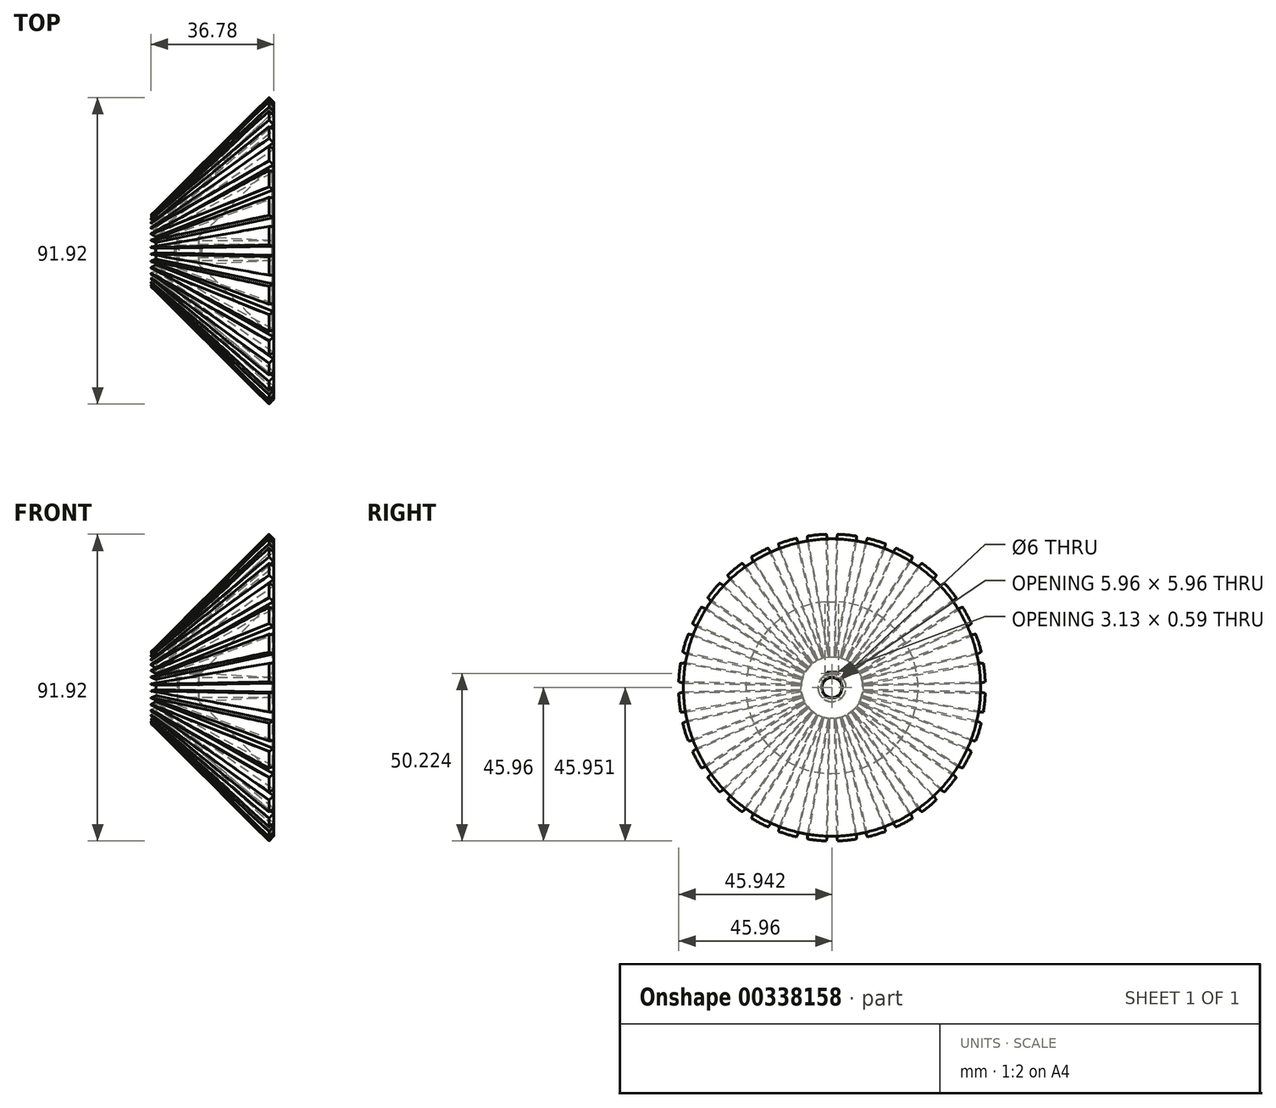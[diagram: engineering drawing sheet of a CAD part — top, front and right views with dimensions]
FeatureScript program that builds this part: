
annotation { "Feature Type Name" : "Feature", "Feature Type Description" : "" }
export const myFeature = defineFeature(function(context is Context, id is Id, definition is map)
    precondition{}
    {
        {
            var Q0;
            Q0=qCreatedBy(makeId("Front.planeOp"),FACE);
            var sketch = newSketch(context, id + "F0", { "sketchPlane" : qUnion([Q0])});
            skLineSegment(sketch, "E0", {"start": v(0, 0) * mm, "end": v(35.34, 35.34) * mm});
            skLineSegment(sketch, "E1", {"start": v(0, 0) * mm, "end": v(38.3, 0) * mm});
            skLineSegment(sketch, "E2", {"start": v(0, 0) * mm, "end": v(-10.6, 10.6) * mm});
            skLineSegment(sketch, "E3", {"start": v(-10.6, 10.6) * mm, "end": v(24.73, 45.94) * mm});
            skLineSegment(sketch, "E4", {"start": v(24.73, 45.94) * mm, "end": v(35.34, 35.34) * mm});
            skSolve(sketch);
        }
        {
            var Q0;
            Q0=makeQuery(id+"F0.imprint","IMPRINT",FACE,{"disambiguationData":[TD([[makeQuery(id+"F0.imprint","IMPRINT",EDGE,{"derivedFrom":sQuery(id+"F0.wireOp",EDGE,"E0")}),1.0]])]});
            extrude(context, id + "F1", {"entities" : qUnion([Q0]), "endBound" : BoundingType.SYMMETRIC, "depth" : 4 * mm});
        }
        {
            var Q0;
            Q0=makeQuery(id+"F1.opExtrude","SWEPT_FACE",FACE,{"disambiguationData":[OSD([sQuery(id+"F0.wireOp",EDGE,"E3")])]});
            var sketch = newSketch(context, id + "F2", { "sketchPlane" : qUnion([Q0])});
            skPoint(sketch, "E5", {"position": v(-2, 49.97) * mm});
            skPoint(sketch, "E6", {"position": v(-1, -0.02) * mm});
            skLineSegment(sketch, "E7", {"start": v(-1, -0.02) * mm, "end": v(1, 0.02) * mm, "construction": true});
            skPoint(sketch, "E8", {"position": v(0, 0) * mm});
            skLineSegment(sketch, "E9", {"start": v(0, -8) * mm, "end": v(0, -12.28) * mm, "construction": true});
            skLineSegment(sketch, "E10", {"start": v(1.74, 52.97) * mm, "end": v(-1.74, 52.97) * mm});
            skLineSegment(sketch, "E11", {"start": v(0.94, -3.02) * mm, "end": v(-0.94, -3.02) * mm});
            skLineSegment(sketch, "E12", {"start": v(-0.94, -3.02) * mm, "end": v(-1.74, 52.97) * mm});
            skLineSegment(sketch, "E13.MirrorCS", {"start": v(0.94, -3.02) * mm, "end": v(1.74, 52.97) * mm});
            skSolve(sketch);
        }
        {
            var Q0;
            Q0=qCreatedBy(makeId("Top.planeOp"),FACE);
            var sketch = newSketch(context, id + "F3", { "sketchPlane" : qUnion([Q0])});
            skLineSegment(sketch, "E14", {"start": v(0, 0) * mm, "end": v(0, -17.72) * mm});
            skLineSegment(sketch, "E15", {"start": v(0, 0) * mm, "end": v(21.3, 0) * mm});
            skSolve(sketch);
        }
        {
            var Q0;
            Q0=makeQuery(id+"F1.opExtrude","CAP_FACE",FACE,{"disambiguationData":[OSD([sQuery(id+"F0.wireOp",EDGE,"E0"),sQuery(id+"F0.wireOp",EDGE,"E2"),sQuery(id+"F0.wireOp",EDGE,"E3"),sQuery(id+"F0.wireOp",EDGE,"E4")])],"isStart":false});
            var Q1;
            Q1=sQuery(id+"F3.wireOp",EDGE,"E15");
            revolve(context, id + "F4", {"operationType" : NewBodyOperationType.ADD, "entities" : qUnion([Q0]), "axis" : qUnion([Q1]), "revolveType" : RevolveType.FULL});
        }
        {
            var Q0;
            {var subQ0=sQuery(id+"F2.wireOp",EDGE,"E12");var subQ1=sQuery(id+"F0.wireOp",EDGE,"E3");var subQ2=makeQuery(id+"F1.opExtrude","SWEPT_EDGE",EDGE,{"disambiguationData":[OSD([sQuery(id+"F0.wireOp",EDGE,"E2"),subQ1])]});var subQ3=makeQuery(id+"F2.imprint","INTERSECT",VERTEX,{"derivedFrom":[subQ2,subQ0]});Q0=makeQuery(id+"F2.imprint","IMPRINT",FACE,{"disambiguationData":[TD([[makeQuery(id+"F2.imprint","IMPRINT",EDGE,{"disambiguationData":[TD([[subQ3,-1.0]])],"derivedFrom":subQ0}),-1.0]])]});}
            var Q1;
            {var subQ0=sQuery(id+"F2.wireOp",EDGE,"E11");Q1=makeQuery(id+"F2.imprint","IMPRINT",FACE,{"disambiguationData":[TD([[makeQuery(id+"F2.imprint","IMPRINT",EDGE,{"derivedFrom":subQ0}),-1.0]])]});}
            var Q2;
            {var subQ0=sQuery(id+"F2.wireOp",EDGE,"E10");Q2=makeQuery(id+"F2.imprint","IMPRINT",FACE,{"disambiguationData":[TD([[makeQuery(id+"F2.imprint","IMPRINT",EDGE,{"derivedFrom":subQ0}),1.0]])]});}
            extrude(context, id + "F5", {"entities" : qUnion([Q0, Q1, Q2]), "oppositeDirection" : true, "depth" : 2 * mm, "hasDraft" : true, "draftAngle" : 10 * degree, "draftPullDirection" : true, "hasSecondDirection" : true, "secondDirectionOppositeDirection" : false, "secondDirectionDepth" : 1 * mm});
        }
        {
            var Q0;
            Q0=makeQuery(id+"F5.opExtrude","SWEPT_BODY",BODY,{"disambiguationData":[OSD([sQuery(id+"F2.wireOp",EDGE,"E10"),sQuery(id+"F2.wireOp",EDGE,"E11"),sQuery(id+"F2.wireOp",EDGE,"E12"),sQuery(id+"F2.wireOp",EDGE,"E13.MirrorCS")])]});
            var Q1;
            Q1=sQuery(id+"F3.wireOp",EDGE,"E15");
            circularPattern(context, id + "F6", {"operationType" : NewBodyOperationType.REMOVE, "entities" : qUnion([Q0]), "axis" : qUnion([Q1]), "angle" : 360 * degree, "instanceCount" : 32, "equalSpace" : true});
        }
        {
            var Q0;
            Q0=qCreatedBy(makeId("Right.planeOp"),FACE);
            var sketch = newSketch(context, id + "F7", { "sketchPlane" : qUnion([Q0])});
            skCircle(sketch, "E16", {"center": v(0, 0) * mm, "radius": 35.4 * mm});
            skPoint(sketch, "E17", {"position": v(0, 45.94) * mm});
            skCircle(sketch, "E18", {"center": v(0, 0) * mm, "radius": 3 * mm});
            skSolve(sketch);
        }
        {
            var Q0;
            Q0=makeQuery(id+"F7.imprint","IMPRINT",FACE,{"disambiguationData":[TD([[makeQuery(id+"F7.imprint","IMPRINT",EDGE,{"derivedFrom":sQuery(id+"F7.wireOp",EDGE,"E16")}),1.0]])]});
            var Q1;
            Q1=sQuery(id+"F0.wireOp",VERTEX,"E4.end");
            extrude(context, id + "F8", {"entities" : qUnion([Q0]), "operationType" : NewBodyOperationType.ADD, "endBound" : BoundingType.UP_TO_VERTEX, "endBoundEntityVertex" : qUnion([Q1]), "depth" : 56.9 * mm, "hasSecondDirection" : true, "secondDirectionOppositeDirection" : false, "secondDirectionDepth" : 25.7 * mm});
        }
        {
            var Q0;
            Q0=qCreatedBy(makeId("Top.planeOp"),FACE);
            var sketch = newSketch(context, id + "F9", { "sketchPlane" : qUnion([Q0])});
            skLineSegment(sketch, "E19.bottom", {"start": v(26.17, 74.13) * mm, "end": v(56.17, 74.13) * mm});
            skLineSegment(sketch, "E19.top", {"start": v(26.17, -66.7) * mm, "end": v(56.17, -66.7) * mm});
            skLineSegment(sketch, "E19.left", {"start": v(26.17, 74.13) * mm, "end": v(26.17, -66.7) * mm});
            skLineSegment(sketch, "E19.right", {"start": v(56.17, 74.13) * mm, "end": v(56.17, -66.7) * mm});
            skSolve(sketch);
        }
        {
            var Q0;
            Q0=makeQuery(id+"F9.imprint","IMPRINT",FACE,{"disambiguationData":[TD([[makeQuery(id+"F9.imprint","IMPRINT",EDGE,{"derivedFrom":sQuery(id+"F9.wireOp",EDGE,"E19.bottom")}),-1.0]])]});
            extrude(context, id + "F10", {"entities" : qUnion([Q0]), "operationType" : NewBodyOperationType.REMOVE, "endBound" : BoundingType.SYMMETRIC, "oppositeDirection" : true, "depth" : 112 * mm});
        }
        {
            var Q0;
            Q0=qCreatedBy(makeId("Right.planeOp"),FACE);
            var sketch = newSketch(context, id + "F11", { "sketchPlane" : qUnion([Q0])});
            skCircle(sketch, "E20", {"center": v(0, 0) * mm, "radius": 10.6 * mm});
            skPoint(sketch, "E21", {"position": v(0, 10.6) * mm});
            skCircle(sketch, "E22", {"center": v(0, 0) * mm, "radius": 3 * mm});
            skLineSegment(sketch, "E23.bottom", {"start": v(1.56, 2.56) * mm, "end": v(-1.56, 2.56) * mm, "construction": true});
            skLineSegment(sketch, "E23.top", {"start": v(1.56, -1.18) * mm, "end": v(-1.56, -1.18) * mm});
            skLineSegment(sketch, "E23.left", {"start": v(1.56, 2.56) * mm, "end": v(1.56, -1.18) * mm});
            skLineSegment(sketch, "E23.right", {"start": v(-1.56, 2.56) * mm, "end": v(-1.56, -1.18) * mm});
            skPoint(sketch, "E24", {"position": v(0, 2.56) * mm});
            skLineSegment(sketch, "E25.top", {"start": v(1.56, 4.56) * mm, "end": v(-1.56, 4.56) * mm});
            skLineSegment(sketch, "E25.left", {"start": v(1.56, -1.18) * mm, "end": v(1.56, 4.56) * mm});
            skLineSegment(sketch, "E25.right", {"start": v(-1.56, -1.18) * mm, "end": v(-1.56, 4.56) * mm});
            skSolve(sketch);
        }
        {
            var Q0;
            Q0=makeQuery(id+"F11.imprint","IMPRINT",FACE,{"disambiguationData":[TD([[makeQuery(id+"F11.imprint","IMPRINT",EDGE,{"derivedFrom":sQuery(id+"F11.wireOp",EDGE,"E20")}),1.0]])]});
            var Q1;
            {var subQ5=sQuery(id+"F11.wireOp",EDGE,"E23.top");Q1=makeQuery(id+"F11.imprint","IMPRINT",FACE,{"disambiguationData":[TD([[makeQuery(id+"F11.imprint","IMPRINT",EDGE,{"derivedFrom":subQ5}),1.0]])]});}
            var Q2;
            {var subQ5=sQuery(id+"F11.wireOp",EDGE,"E23.top");Q2=makeQuery(id+"F11.imprint","IMPRINT",FACE,{"disambiguationData":[TD([[makeQuery(id+"F11.imprint","IMPRINT",EDGE,{"derivedFrom":subQ5}),-1.0]])]});}
            var Q3;
            {var subQ5=sQuery(id+"F11.wireOp",EDGE,"E25.top");Q3=makeQuery(id+"F11.imprint","IMPRINT",FACE,{"disambiguationData":[TD([[makeQuery(id+"F11.imprint","IMPRINT",EDGE,{"derivedFrom":subQ5}),1.0]])]});}
            extrude(context, id + "F12", {"entities" : qUnion([Q0, Q1, Q2, Q3]), "operationType" : NewBodyOperationType.ADD, "oppositeDirection" : true, "depth" : 9 * mm, "hasDraft" : true, "draftAngle" : 8 * degree, "draftPullDirection" : true});
        }
        {
            var Q0;
            Q0=makeQuery(id+"F12.opExtrude","CAP_FACE",FACE,{"disambiguationData":[OSD([sQuery(id+"F11.wireOp",EDGE,"E20")])],"isStart":false});
            var sketch = newSketch(context, id + "F13", { "sketchPlane" : qUnion([Q0])});
            skCircle(sketch, "E26", {"center": v(0, 0) * mm, "radius": 3 * mm});
            skLineSegment(sketch, "E27.bottom", {"start": v(-1.56, 4.56) * mm, "end": v(1.56, 4.56) * mm});
            skLineSegment(sketch, "E27.top", {"start": v(-1.56, 2) * mm, "end": v(1.56, 2) * mm, "construction": true});
            skLineSegment(sketch, "E27.left", {"start": v(-1.56, 4.56) * mm, "end": v(-1.56, 2) * mm});
            skLineSegment(sketch, "E27.right", {"start": v(1.56, 4.56) * mm, "end": v(1.56, 2) * mm});
            skSolve(sketch);
        }
        {
            var Q0;
            Q0=makeQuery(id+"F10.boolean.opBoolean","COPY",FACE,{"derivedFrom":makeQuery(id+"F10.opExtrude","SWEPT_FACE",FACE,{"disambiguationData":[OSD([sQuery(id+"F9.wireOp",EDGE,"E19.left")])]})});
            var sketch = newSketch(context, id + "F14", { "sketchPlane" : qUnion([Q0])});
            skCircle(sketch, "E28", {"center": v(0, 0) * mm, "radius": 3 * mm});
            skSolve(sketch);
        }
        {
            var Q0;
            Q0=makeQuery(id+"F14.imprint","IMPRINT",FACE,{"disambiguationData":[TD([[makeQuery(id+"F14.imprint","IMPRINT",EDGE,{"derivedFrom":sQuery(id+"F14.wireOp",EDGE,"E28")}),-1.0]])]});
            var Q1;
            Q1=sQuery(id+"F11.wireOp",VERTEX,"E21");
            extrude(context, id + "F15", {"entities" : qUnion([Q0]), "operationType" : NewBodyOperationType.ADD, "endBound" : BoundingType.UP_TO_VERTEX, "oppositeDirection" : true, "endBoundEntityVertex" : qUnion([Q1]), "depth" : 25 * mm, "hasDraft" : true, "draftAngle" : 3 * degree});
        }
        {
            var Q0;
            {var subQ5=sQuery(id+"F13.wireOp",EDGE,"E27.bottom");Q0=makeQuery(id+"F13.imprint","IMPRINT",FACE,{"disambiguationData":[TD([[makeQuery(id+"F13.imprint","IMPRINT",EDGE,{"derivedFrom":subQ5}),-1.0]])]});}
            var Q1;
            {var subQ0=sQuery(id+"F13.wireOp",EDGE,"E26");var subQ1=makeQuery(id+"F13.imprint","INTERSECT",VERTEX,{"derivedFrom":[subQ0,sQuery(id+"F13.wireOp",EDGE,"E27.left")]});Q1=makeQuery(id+"F13.imprint","IMPRINT",FACE,{"disambiguationData":[TD([[makeQuery(id+"F13.imprint","IMPRINT",EDGE,{"disambiguationData":[TD([[subQ1,1.0]])],"derivedFrom":subQ0}),1.0]])]});}
            extrude(context, id + "F16", {"entities" : qUnion([Q0, Q1]), "operationType" : NewBodyOperationType.REMOVE, "oppositeDirection" : true, "depth" : 288.6 * mm});
        }
    });
